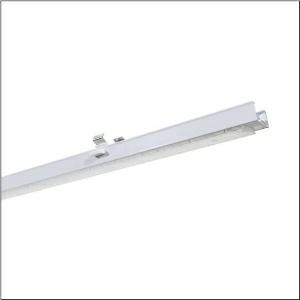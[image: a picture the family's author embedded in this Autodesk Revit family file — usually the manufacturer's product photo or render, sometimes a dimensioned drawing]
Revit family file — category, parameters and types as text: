
# Revit family: trunking_flex_31_51re12ma46b
name_source: partatom
category: Lighting Fixtures
units: mm (PartAtom-declared; Revit-internal decimal feet)

## family parameters
Cut with Voids When Loaded = No
Host = Face
Light Source = No
Part Type = Normal
Room Calculation Point = No
Round Connector Dimension = Use Diameter
Shared = No

## types (1)
- --- (1 x LED, 6400 lm, 40 W, 4000K)
    Apparent Load = 40 VA
    CIE Flux Codes = 65 91 98 99 100
    Color Rendering = 80
    Color Temperature = 4000K
    Default Elevation = 1800 mm
    Description = Trunking Flex 31, luminaire insert, of extruded aluminium section, coated, traffic white (RAL 9016), length: 1.172mm, width: 91mm, height: 53mm, LED rated luminous flux: 6.400lm, light colour: 840, control gear: ON/OFF Multilumen, with system connector: socket, mains connection: 220..240V, AC, 50/60Hz, rated input power: 40W, luminous flux adjustable on luminaire in four steps (3420/4540/5580/6630lm), connected load according to luminous flux setting (20/26/33/40W), primary light control with lens, of plastic, primary optical cover: cover, of PMMA, light emission: direct distribution, protection rating (complete): IP20, insulation class (complete): insulation class I (protective earthing), certification: CE, UKCA, impact resistance: IK02, permissible ambient temperature for indoor applications: -20..+40°C, packaging unit: 1 piece
    Height = 58 mm
    Lamp = 1 x LED
    Lamp Light Flux = 6400 lm
    Lamp Power = 40 W
    Lamp count = 1
    Length = 1172 mm
    Luminous efficacy = 160 lm/W
    Manufacturer = Siteco
    ModVariant = No
    Model = 51RE12MA46B
    Mounting Place = Ceiling
    Mounting Type = Pendant
    Number of Poles = 1
    OnlyDefault = Yes
    Power Factor = 1
    Product Name = Trunking Flex 31
    Product group = luminaire insert | ceiling pendant
    ProductGroupID = 902
    Protection Class = Protection class I
    Protection Degree = IP 20
    RLX_Detail_Level = 1
    RLX_Emergency_Light_Flux = 0 lm
    RLX_Emergency_Type = 0
    RLX_Emergency_Type_DB = No
    RlxData = <blob elided: 19981 chars, md5=cf70e42f>
    Socket = socket
    Standby Power = 0 W
    System Light Flux = 6400 lm
    System Power = 40 W
    Type Comments = factory setting: luminous flux: 100 % | (ON | ON) | 300 mA
    Type Image = l_1266702.jpg
    URL = http://relux.com
    VarID = @adj_079275
    Voltage = 0 V
    Weight = 0.00 kg
    Width = 65 mm

## geometry (parser evidence)
native form markers: Blend x4, Sweep x11
no freeform markers — native parametric forms only
